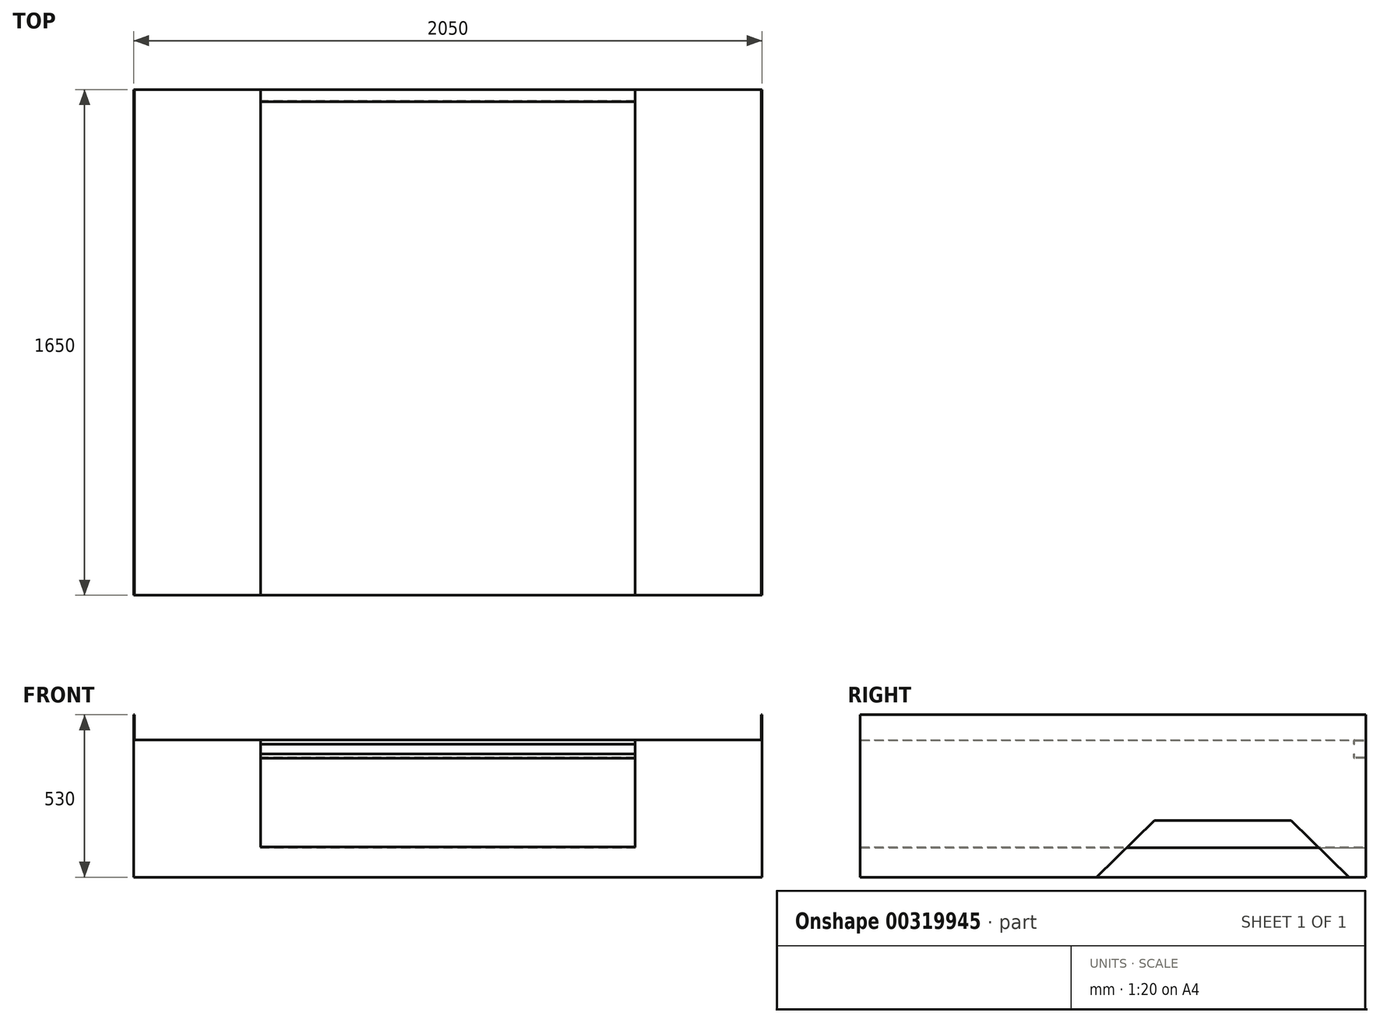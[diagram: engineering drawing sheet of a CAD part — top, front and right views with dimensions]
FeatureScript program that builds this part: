
annotation { "Feature Type Name" : "Feature", "Feature Type Description" : "" }
export const myFeature = defineFeature(function(context is Context, id is Id, definition is map)
    precondition{}
    {
        {
            var Q0;
            Q0=qCreatedBy(makeId("Front.planeOp"),FACE);
            var sketch = newSketch(context, id + "F0", { "sketchPlane" : qUnion([Q0])});
            skLineSegment(sketch, "E0", {"start": v(0, 0) * mm, "end": v(0, 530) * mm, "construction": true});
            skLineSegment(sketch, "E1.bottom", {"start": v(1025, 0) * mm, "end": v(-1025, 0) * mm});
            skLineSegment(sketch, "E1.top", {"start": v(1025, 530) * mm, "end": v(1022, 530) * mm});
            skLineSegment(sketch, "E1.left", {"start": v(1025, 0) * mm, "end": v(1025, 530) * mm});
            skLineSegment(sketch, "E1.right", {"start": v(-1025, 0) * mm, "end": v(-1025, 530) * mm});
            skLineSegment(sketch, "E2.top", {"start": v(-611, 98) * mm, "end": v(611, 98) * mm});
            skLineSegment(sketch, "E2.left", {"start": v(-611, 448) * mm, "end": v(-611, 98) * mm});
            skLineSegment(sketch, "E2.right", {"start": v(611, 448) * mm, "end": v(611, 98) * mm});
            skLineSegment(sketch, "E3.top", {"start": v(-1022, 448) * mm, "end": v(-611, 448) * mm});
            skLineSegment(sketch, "E3.left", {"start": v(-1022, 530) * mm, "end": v(-1022, 448) * mm});
            skLineSegment(sketch, "E3.right", {"start": v(1022, 530) * mm, "end": v(1022, 448) * mm});
            skLineSegment(sketch, "E4.trimOffspring", {"start": v(-1022, 530) * mm, "end": v(-1025, 530) * mm});
            skLineSegment(sketch, "E5.trimOffspring", {"start": v(611, 448) * mm, "end": v(1022, 448) * mm});
            skLineSegment(sketch, "E6", {"start": v(-1025, 530) * mm, "end": v(1125, 530) * mm, "construction": true});
            skSolve(sketch);
        }
        {
            var Q0;
            Q0 = qSketchRegion(id + "F0", true);
            var Q1;
            Q1 = qConstructionFilter(qBodyType(qCreatedBy(id + "F0" ,EDGE), BodyType.WIRE), ConstructionObject.NO);
            extrude(context, id + "F1", {"entities" : qUnion([Q0]), "surfaceEntities" : qUnion([Q1]), "depth" : 1650 * mm});
        }
        {
            var Q0;
            Q0=makeQuery(id+"F1.opExtrude","SWEPT_FACE",FACE,{"disambiguationData":[OSD([sQuery(id+"F0.wireOp",EDGE,"E1.bottom")])]});
            shell(context, id + "F2", {"entities" : qUnion([Q0]), "thickness" : 1.5 * mm});
        }
        {
            var Q0;
            Q0=qCreatedBy(makeId("Right.planeOp"),FACE);
            var sketch = newSketch(context, id + "F3", { "sketchPlane" : qUnion([Q0])});
            skLineSegment(sketch, "E7", {"start": v(0, 445) * mm, "end": v(0, 391) * mm});
            skLineSegment(sketch, "E8", {"start": v(-3, 388) * mm, "end": v(-37, 388) * mm});
            skLineSegment(sketch, "E9", {"start": v(-40, 391) * mm, "end": v(-40, 402) * mm});
            skLineSegment(sketch, "E10", {"start": v(-40, 434) * mm, "end": v(-40, 445) * mm});
            skLineSegment(sketch, "E11", {"start": v(-37, 448) * mm, "end": v(-3, 448) * mm});
            skPoint(sketch, "E12.visualSharp", {"position": v(-40, 448) * mm});
            skArc(sketch, "E12.filletArc", {"start": v(-37, 448) * mm, "mid": v(-39.12, 447.12) * mm, "end": v(-40, 445) * mm});
            skPoint(sketch, "E13.visualSharp", {"position": v(0, 448) * mm});
            skArc(sketch, "E13.filletArc", {"start": v(0, 445) * mm, "mid": v(-0.88, 447.12) * mm, "end": v(-3, 448) * mm});
            skPoint(sketch, "E14.visualSharp", {"position": v(0, 388) * mm});
            skArc(sketch, "E14.filletArc", {"start": v(-3, 388) * mm, "mid": v(-0.88, 388.88) * mm, "end": v(0, 391) * mm});
            skPoint(sketch, "E15.visualSharp", {"position": v(-40, 388) * mm});
            skArc(sketch, "E15.filletArc", {"start": v(-40, 391) * mm, "mid": v(-39.12, 388.88) * mm, "end": v(-37, 388) * mm});
            skLineSegment(sketch, "E16.0", {"start": v(-37, 391) * mm, "end": v(-37, 402) * mm});
            skLineSegment(sketch, "E16.1", {"start": v(-37, 434) * mm, "end": v(-37, 445) * mm});
            skLineSegment(sketch, "E16.2", {"start": v(-37, 445) * mm, "end": v(-3, 445) * mm});
            skLineSegment(sketch, "E16.3", {"start": v(-3, 445) * mm, "end": v(-3, 391) * mm});
            skLineSegment(sketch, "E16.4", {"start": v(-3, 391) * mm, "end": v(-37, 391) * mm});
            skLineSegment(sketch, "E17.0", {"start": v(-1645, 525) * mm, "end": v(-1645, 5) * mm});
            skLineSegment(sketch, "E17.1", {"start": v(-1645, 525) * mm, "end": v(5, 525) * mm});
            skLineSegment(sketch, "E17.2", {"start": v(5, 5) * mm, "end": v(5, 525) * mm});
            skLineSegment(sketch, "E17.3", {"start": v(5, 5) * mm, "end": v(-1645, 5) * mm});
            skLineSegment(sketch, "E18", {"start": v(-40, 434) * mm, "end": v(-37, 434) * mm});
            skLineSegment(sketch, "E19", {"start": v(-40, 402) * mm, "end": v(-37, 402) * mm});
            skSolve(sketch);
        }
        {
            var Q0;
            Q0=makeQuery(id+"F3.imprint","IMPRINT",FACE,{"disambiguationData":[TD([[makeQuery(id+"F3.imprint","IMPRINT",EDGE,{"derivedFrom":sQuery(id+"F3.wireOp",EDGE,"E9")}),-1.0]])]});
            var Q1;
            Q1=makeQuery(id+"F3.imprint","IMPRINT",FACE,{"disambiguationData":[TD([[makeQuery(id+"F3.imprint","IMPRINT",EDGE,{"derivedFrom":sQuery(id+"F3.wireOp",EDGE,"E10")}),-1.0]])]});
            var Q2;
            Q2=makeQuery(id+"F3.imprint","IMPRINT",FACE,{"disambiguationData":[TD([[makeQuery(id+"F3.imprint","IMPRINT",EDGE,{"derivedFrom":sQuery(id+"F3.wireOp",EDGE,"E7")}),-1.0]])]});
            var Q3;
            Q3=makeQuery(id+"F1.opExtrude","SWEPT_FACE",FACE,{"disambiguationData":[OSD([sQuery(id+"F0.wireOp",EDGE,"E2.right")])]});
            var Q4;
            Q4=makeQuery(id+"F1.opExtrude","SWEPT_FACE",FACE,{"disambiguationData":[OSD([sQuery(id+"F0.wireOp",EDGE,"E2.left")])]});
            extrude(context, id + "F4", {"entities" : qUnion([Q0, Q1, Q2]), "endBound" : BoundingType.UP_TO_SURFACE, "endBoundEntityFace" : qUnion([Q3]), "depth" : 25 * mm, "hasSecondDirection" : true, "secondDirectionBound" : SecondDirectionBoundingType.UP_TO_SURFACE, "secondDirectionOppositeDirection" : true, "secondDirectionBoundEntityFace" : qUnion([Q4]), "secondDirectionDepth" : 25 * mm});
        }
        {
            var Q0;
            Q0=qCreatedBy(makeId("Right.planeOp"),FACE);
            var sketch = newSketch(context, id + "F5", { "sketchPlane" : qUnion([Q0])});
            skPoint(sketch, "E20.0", {"position": v(0, 0) * mm});
            skLineSegment(sketch, "E21.0", {"start": v(0, 448) * mm, "end": v(0, 0) * mm});
            skLineSegment(sketch, "E22.0", {"start": v(0, 0) * mm, "end": v(-1650, 0) * mm, "construction": true});
            skPoint(sketch, "E23.orphan", {"position": v(0, 98) * mm});
            skLineSegment(sketch, "E24", {"start": v(0, 0) * mm, "end": v(-60, 0) * mm});
            skSolve(sketch);
        }
        {
            var Q0;
            Q0=sQuery(id+"F5.wireOp",EDGE,"E21.0");
            var Q1;
            Q1=sQuery(id+"F5.wireOp",EDGE,"E24");
            var Q2;
            Q2=makeQuery(id+"F1.opExtrude","SWEPT_FACE",FACE,{"disambiguationData":[OSD([sQuery(id+"F0.wireOp",EDGE,"E1.left")])]});
            var Q3;
            Q3=makeQuery(id+"F1.opExtrude","SWEPT_FACE",FACE,{"disambiguationData":[OSD([sQuery(id+"F0.wireOp",EDGE,"E1.right")])]});
            extrude(context, id + "F6", {"bodyType" : ToolBodyType.SURFACE, "surfaceEntities" : qUnion([Q0, Q1]), "endBound" : BoundingType.UP_TO_SURFACE, "endBoundEntityFace" : qUnion([Q2]), "depth" : 25 * mm, "hasSecondDirection" : true, "secondDirectionBound" : SecondDirectionBoundingType.UP_TO_SURFACE, "secondDirectionOppositeDirection" : true, "secondDirectionBoundEntityFace" : qUnion([Q3]), "secondDirectionDepth" : 25 * mm});
        }
        {
            var Q0;
            Q0=makeQuery(id+"F1.opExtrude","SWEPT_FACE",FACE,{"disambiguationData":[OSD([sQuery(id+"F0.wireOp",EDGE,"E1.left")])]});
            var sketch = newSketch(context, id + "F7", { "sketchPlane" : qUnion([Q0])});
            skLineSegment(sketch, "E25", {"start": v(-55, 0) * mm, "end": v(-244.74, 185) * mm});
            skLineSegment(sketch, "E26", {"start": v(-244.74, 185) * mm, "end": v(-689.74, 185) * mm});
            skLineSegment(sketch, "E27", {"start": v(-879.47, 0) * mm, "end": v(-689.74, 185) * mm});
            skLineSegment(sketch, "E28", {"start": v(-467.24, 185) * mm, "end": v(-467.24, 0) * mm, "construction": true});
            skSolve(sketch);
        }
        {
            var Q0;
            {var subQ0=sQuery(id+"F7.wireOp",EDGE,"E25");Q0=makeQuery(id+"F7.imprint","IMPRINT",FACE,{"disambiguationData":[TD([[makeQuery(id+"F7.imprint","IMPRINT",EDGE,{"derivedFrom":subQ0}),1.0]])]});}
            extrude(context, id + "F8", {"entities" : qUnion([Q0]), "operationType" : NewBodyOperationType.REMOVE, "endBound" : BoundingType.UP_TO_NEXT, "oppositeDirection" : true, "depth" : 25 * mm});
        }
    });
